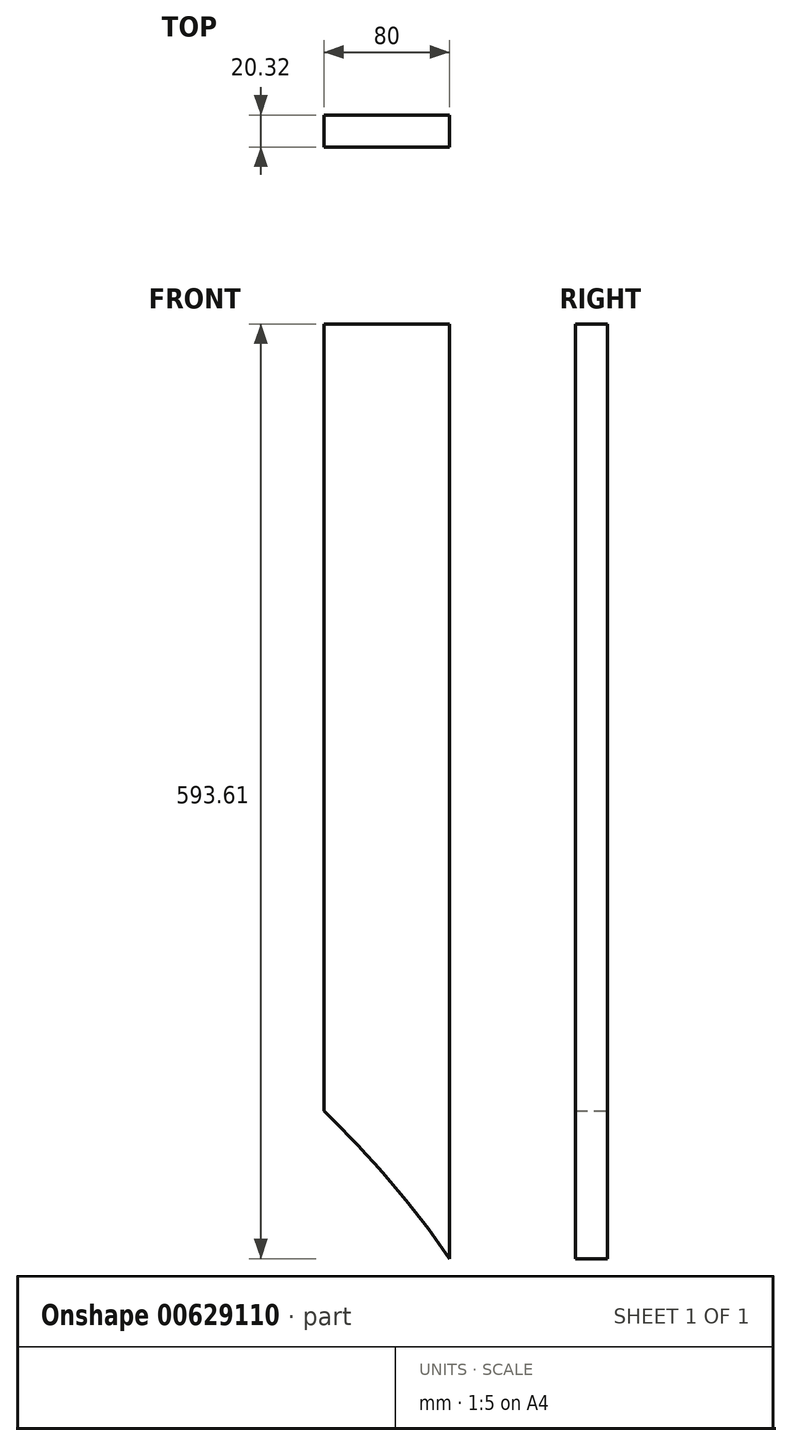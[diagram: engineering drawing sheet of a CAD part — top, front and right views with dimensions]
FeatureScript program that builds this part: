
annotation { "Feature Type Name" : "Feature", "Feature Type Description" : "" }
export const myFeature = defineFeature(function(context is Context, id is Id, definition is map)
    precondition{}
    {
        {
            var Q0;
            Q0=qCreatedBy(makeId("Front.planeOp"),FACE);
            var sketch = newSketch(context, id + "F0", { "sketchPlane" : qUnion([Q0])});
            skLineSegment(sketch, "E0.bottom", {"start": v(-320, 160) * mm, "end": v(320, 160) * mm});
            skLineSegment(sketch, "E0.top", {"start": v(-320, -160) * mm, "end": v(320, -160) * mm});
            skLineSegment(sketch, "E0.left", {"start": v(-320, 160) * mm, "end": v(-320, -160) * mm});
            skPoint(sketch, "E0.middle", {"position": v(0, 0) * mm});
            skArc(sketch, "E1", {"start": v(639.99, -480) * mm, "mid": v(546.27, -253.73) * mm, "end": v(320, -160.01) * mm});
            skArc(sketch, "E2.0", {"start": v(959.98, -480) * mm, "mid": v(772.53, -27.47) * mm, "end": v(320, 159.98) * mm});
            skLineSegment(sketch, "E3.top", {"start": v(639.99, -1120) * mm, "end": v(959.98, -1120) * mm});
            skLineSegment(sketch, "E3.left", {"start": v(639.99, -480) * mm, "end": v(639.99, -1120) * mm});
            skLineSegment(sketch, "E3.right", {"start": v(959.98, -480) * mm, "end": v(959.98, -1120) * mm});
            skPoint(sketch, "E4.middle", {"position": v(799.72, 166.76) * mm});
            skLineSegment(sketch, "E5", {"start": v(804.72, 480) * mm, "end": v(764.72, 480) * mm});
            skLineSegment(sketch, "E6", {"start": v(764.72, 480) * mm, "end": v(764.72, -19.78) * mm});
            skLineSegment(sketch, "E7", {"start": v(764.72, 480) * mm, "end": v(844.72, 480) * mm});
            skLineSegment(sketch, "E8", {"start": v(844.72, 480) * mm, "end": v(844.72, -113.6) * mm});
            skSolve(sketch);
        }
        {
            var Q0;
            {var subQ0=sQuery(id+"F0.wireOp",EDGE,"E6");Q0=makeQuery(id+"F0.imprint","IMPRINT",FACE,{"disambiguationData":[TD([[makeQuery(id+"F0.imprint","IMPRINT",EDGE,{"derivedFrom":subQ0}),1.0]])]});}
            extrude(context, id + "F1", {"entities" : qUnion([Q0]), "endBound" : BoundingType.SYMMETRIC, "depth" : 20.32 * mm, "offsetDistance" : 25.4 * mm});
        }
    });
